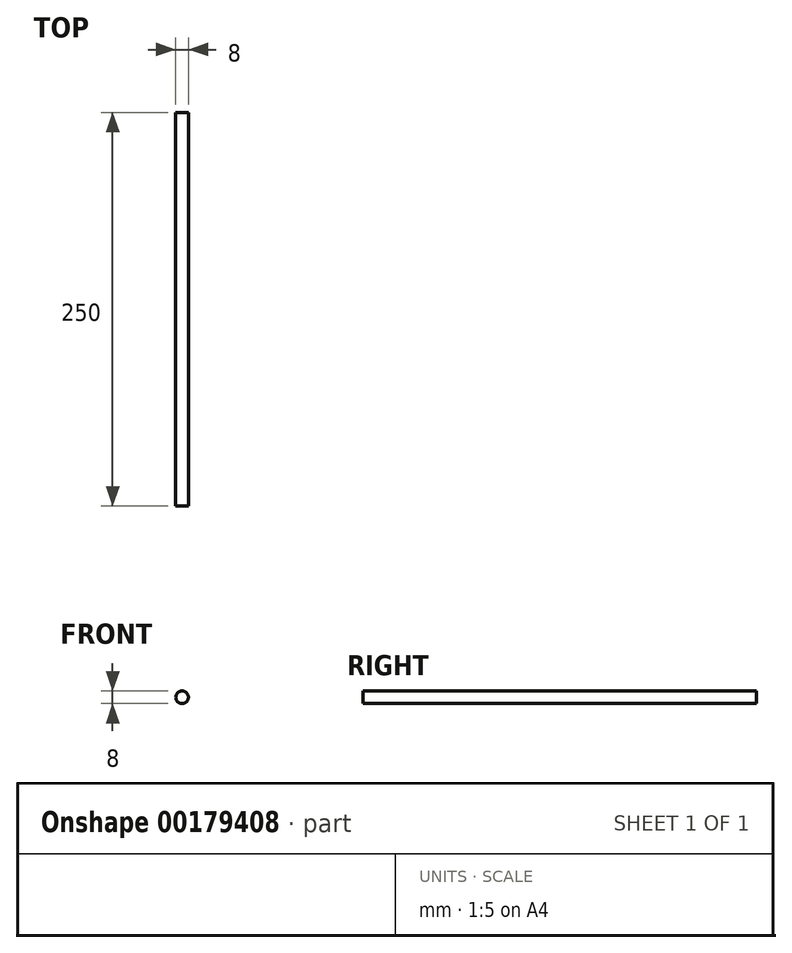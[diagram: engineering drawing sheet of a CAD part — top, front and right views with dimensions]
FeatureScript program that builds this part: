
annotation { "Feature Type Name" : "Feature", "Feature Type Description" : "" }
export const myFeature = defineFeature(function(context is Context, id is Id, definition is map)
    precondition{}
    {
        {
            var Q0;
            Q0=qCreatedBy(makeId("Front.planeOp"),FACE);
            var sketch = newSketch(context, id + "F0", { "sketchPlane" : qUnion([Q0])});
            skCircle(sketch, "E0", {"center": v(0, 0) * mm, "radius": 4 * mm});
            skSolve(sketch);
        }
        {
            var Q0;
            Q0 = qSketchRegion(id + "F0", true);
            extrude(context, id + "F1", {"entities" : qUnion([Q0]), "depth" : 250 * mm});
        }
    });
